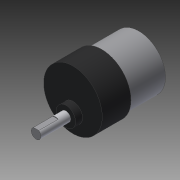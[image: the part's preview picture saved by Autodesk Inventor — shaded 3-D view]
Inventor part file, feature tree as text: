
AUTODESK INVENTOR PART (.ipt)
format: ipt  version: 2014 SP1 (Build 180222100, 222)  size: 165,376 bytes
history: native  units: in
note: dims shown in document units (in); Inventor stores cm internally (conversion verified against a paired STEP export)
features: extrude x7, sketch x7, thread x4
ambient origin geometry x8: Origin, YZ Plane, XZ Plane, XY Plane, X Axis, Y Axis, Z Axis, Center Point
bodies: Solid1 (feature_tree)
feature tree (18):
  extrude  "Extrusion1"  Depth=0.7in TaperAngle=0.0deg
  extrude  "Extrusion2"  Depth=0.47in
  extrude  "Extrusion3"  Depth=0.17in
  extrude  "Extrusion4"  Depth=0.4724in TaperAngle=0.0deg
  extrude  "Extrusion5"  Depth=0.9in TaperAngle=0.0deg
  extrude  "Extrusion6"  Depth=0.125in TaperAngle=0.0deg
  extrude  "Extrusion7"  Depth=0.1181in
  thread  "Thread1"  [1 undecoded]
  thread  "Thread2"  [1 undecoded]
  thread  "Thread3"  [1 undecoded]
  thread  "Thread4"  [1 undecoded]
  sketch  "Sketch1"  dims[d0=1.425in d1=0.7in d2=0.0in]
  sketch  "Sketch2"  dims[d3=0.449in d4=0.47in]
  sketch  "Sketch3"  dims[d5=0.17in d6=0.0in d7=0.2362in]
  sketch  "Sketch4"  dims[d8=0.725in d9=0.0in d11=0.4724in d12=0.0in]
  sketch  "Sketch5"  dims[d13=1.3in d14=0.9in d15=0.0in]
  sketch  "Sketch6"  dims[d16=0.35in d17=0.125in d18=0.0in]
  sketch  "Sketch7"  dims[d21=0.1181in d22=0.1181in d23=2.114in d24=2.114in d25=0.1181in d26=0.1181in d27=0.5in d28=0.0in d29=1.0in d30=0.0in d31=1.0in d32=0.0in d33=1.0in d34=0.0in d35=1.0in d36=0.0in]
note: 4 required parameter values undecoded (feature->parameter linkage not recoverable at this tier; creation-order binding heuristic only, values carry confidence <= 0.55)
